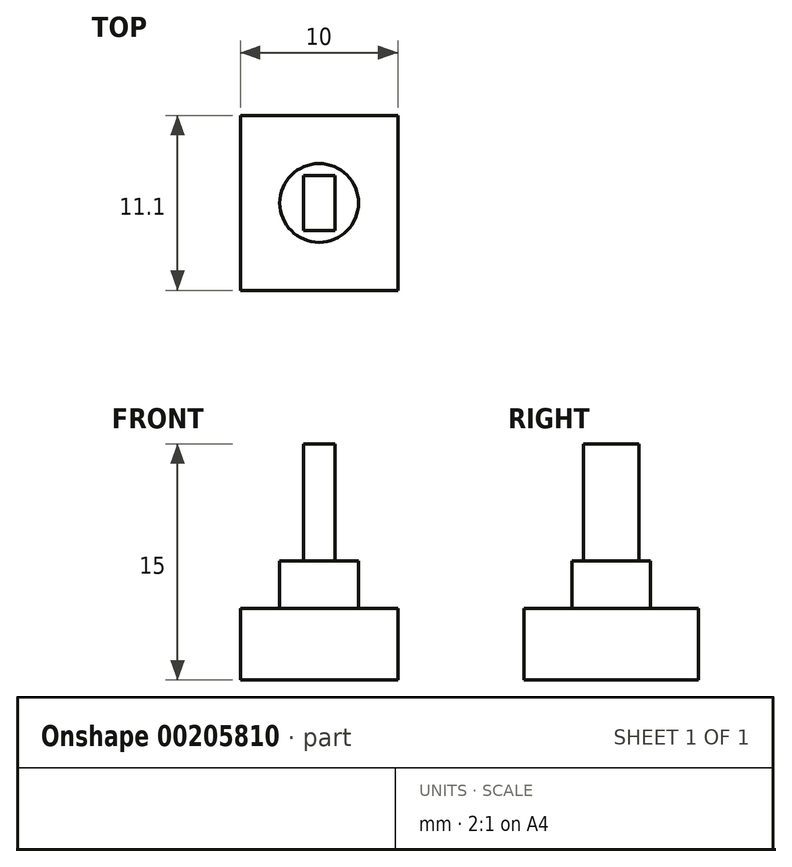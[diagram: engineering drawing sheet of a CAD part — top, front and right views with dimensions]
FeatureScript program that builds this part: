
annotation { "Feature Type Name" : "Feature", "Feature Type Description" : "" }
export const myFeature = defineFeature(function(context is Context, id is Id, definition is map)
    precondition{}
    {
        {
            var Q0;
            Q0=qCreatedBy(makeId("Top.planeOp"),FACE);
            var sketch = newSketch(context, id + "F0", { "sketchPlane" : qUnion([Q0])});
            skLineSegment(sketch, "E0.bottom", {"start": v(5, -5.55) * mm, "end": v(-5, -5.55) * mm});
            skLineSegment(sketch, "E0.top", {"start": v(5, 5.55) * mm, "end": v(-5, 5.55) * mm});
            skLineSegment(sketch, "E0.left", {"start": v(5, -5.55) * mm, "end": v(5, 5.55) * mm});
            skLineSegment(sketch, "E0.right", {"start": v(-5, -5.55) * mm, "end": v(-5, 5.55) * mm});
            skPoint(sketch, "E0.middle", {"position": v(0, 0) * mm});
            skSolve(sketch);
        }
        {
            var Q0;
            Q0=qSketchRegion(id+"F0",true);
            extrude(context, id + "F1", {"entities" : qUnion([Q0]), "depth" : 4.55 * mm});
        }
        {
            var Q0;
            Q0=makeQuery(id+"F1.opExtrude","CAP_FACE",FACE,{"disambiguationData":[OSD([sQuery(id+"F0.wireOp",EDGE,"E0.bottom"),sQuery(id+"F0.wireOp",EDGE,"E0.top"),sQuery(id+"F0.wireOp",EDGE,"E0.left"),sQuery(id+"F0.wireOp",EDGE,"E0.right")])],"isStart":false});
            var sketch = newSketch(context, id + "F2", { "sketchPlane" : qUnion([Q0])});
            skCircle(sketch, "E1", {"center": v(0, 0) * mm, "radius": 2.5 * mm});
            skSolve(sketch);
        }
        {
            var Q0;
            Q0=qSketchRegion(id+"F2",true);
            extrude(context, id + "F3", {"entities" : qUnion([Q0]), "operationType" : NewBodyOperationType.ADD, "depth" : 3 * mm});
        }
        {
            var Q0;
            Q0=makeQuery(id+"F3.opExtrude","CAP_FACE",FACE,{"disambiguationData":[OSD([sQuery(id+"F2.wireOp",EDGE,"E1")])],"isStart":false});
            var sketch = newSketch(context, id + "F4", { "sketchPlane" : qUnion([Q0])});
            skLineSegment(sketch, "E2.bottom", {"start": v(1, 1.75) * mm, "end": v(-1, 1.75) * mm});
            skLineSegment(sketch, "E2.top", {"start": v(1, -1.75) * mm, "end": v(-1, -1.75) * mm});
            skLineSegment(sketch, "E2.left", {"start": v(1, 1.75) * mm, "end": v(1, -1.75) * mm});
            skLineSegment(sketch, "E2.right", {"start": v(-1, 1.75) * mm, "end": v(-1, -1.75) * mm});
            skPoint(sketch, "E2.middle", {"position": v(0, 0) * mm});
            skSolve(sketch);
        }
        {
            var Q0;
            Q0=qSketchRegion(id+"F4",true);
            extrude(context, id + "F5", {"entities" : qUnion([Q0]), "operationType" : NewBodyOperationType.ADD, "depth" : 7.45 * mm});
        }
    });
